# Revit family: Legrand Mini Colonnes clippage direct
name_source: partatom
category: Installations électriques
units: mm (PartAtom-declared; Revit-internal decimal feet)

## family parameters
Basée sur le plan de construction = Non
Conserver l'orientation des annotations = Non
Cote de connecteur circulaire = Utiliser le diamètre
Couper avec des vides une fois chargée = Non
Partagée = Non
Point de calcul de pièce = Non
Toujours verticalement = Oui
Type d'élément = Normal

## types (13) — shared parameters
Fabricant = LEGRAND
Standard = A clippage direct-ON
zero-valued in all types: Elévation par défaut

## per-type parameters (varying)
| type | 1 CPT | 2 CPT | 4 CPT | Black | Column stand | Description | Finition | H1 | HC | Largeur | Longueur | Matériau couvercle | Matériau principal | Matériaux corps | Modèle | Nombre de compartiments | Séparateur |
| Colonnette 1 cpt 45 0,30M BL | Oui | Non | Non | Non | Pied mobile : Pied pour Colonnettes Blanc | Colonnette a clippage direct 1 compartiment 0,30m Blanc | Blanc | 300 mm | 260 mm  [stored 0.853018 ft] | 75 mm  [stored 0.246063 ft] | 82 mm | Legrand - Plastique blanc | Aluminium | Legrand - Aluminium blanc | LG-653000 | 1 compartiment | 35 mm |
| Colonnette 1 cpt 45 0,30M Noir | Oui | Non | Non | Oui | Tablette : Table pour Colonnettes T1/2 | Colonnette a clippage direct 1 compartiment 0,30m Noir | Noir | 300 mm | 260 mm  [stored 0.853018 ft] | 75 mm  [stored 0.246063 ft] | 82 mm | Legrand - Plastique noir | Aluminium | Legrand - Aluminium noir | LG_653002 | 1 compartiment | 35 mm |
| Colonnette 1 cpt 45 0,68M BL | Oui | Non | Non | Non | Pied mobile : Pied pour Colonnettes Blanc | Colonnette a clippage direct 1 compartiment 0,68m Blanc | Blanc | 680 mm  [stored 2.23097 ft] | 640 mm  [stored 2.09974 ft] | 75 mm  [stored 0.246063 ft] | 82 mm | Legrand - Plastique blanc | Aluminium | Legrand - Aluminium blanc | LG-653003 | 1 compartiment | 35 mm |
| Colonnette 1 cpt 45 0,68M Noir | Oui | Non | Non | Oui | Tablette : Table pour Colonnettes T1/2 | Colonnette a clippage direct 1 compartiment 0,68m Noir | Noir | 680 mm  [stored 2.23097 ft] | 640 mm  [stored 2.09974 ft] | 75 mm  [stored 0.246063 ft] | 82 mm | Legrand - Plastique noir | Aluminium | Legrand - Aluminium noir | LG-653005 | 1 compartiment | 35 mm |
| Colonnette 2 cpts 45 0,3M BL | Non | Oui | Non | Non | Pied mobile : Pied pour Colonnettes Blanc | Colonnette a clippage direct 2 compartiments 0,30m Blanc | Blanc | 300 mm | 260 mm  [stored 0.853018 ft] | 75 mm  [stored 0.246063 ft] | 125 mm  [stored 0.410105 ft] | Legrand - Plastique blanc | Plastique | Legrand - Plastique blanc | LG-653020 | 2 compartiments | 35 mm |
| Colonnette 2 cpts 45 0,3M Noir | Non | Oui | Non | Oui | Tablette : Table pour Colonnettes T1/2 | Colonnette a clippage direct 2 compartiments 0,30m Noir | Noir | 300 mm | 260 mm  [stored 0.853018 ft] | 75 mm  [stored 0.246063 ft] | 125 mm  [stored 0.410105 ft] | Legrand - Plastique noir | Aluminium | Legrand - Aluminium noir | LG-653022 | 2 compartiments | 35 mm |
| Colonnette 2 cpts 45 0,68M Blanc | Non | Oui | Non | Non | Pied mobile : Pied pour Colonnettes Blanc | Colonnette a clippage direct 2 compartiments 0,68m Blanc | Blanc | 380 mm | 340 mm | 75 mm  [stored 0.246063 ft] | 125 mm  [stored 0.410105 ft] | Legrand - Plastique blanc | Aluminium | Legrand - Aluminium blanc | LG-653023 | 2 compartiments | 35 mm |
| Colonnette 2 cpt 45 0,68M Noir | Non | Oui | Non | Oui | Tablette : Table pour Colonnettes T1/2 | Colonnette a clippage direct 2 compartiments 0,68m Noir | Noir | 680 mm  [stored 2.23097 ft] | 640 mm  [stored 2.09974 ft] | 75 mm  [stored 0.246063 ft] | 125 mm  [stored 0.410105 ft] | Legrand - Plastique noir | Aluminium | Legrand - Aluminium noir | LG-653025 | 2 compartiments | 35 mm |
| Colonnette 4 cpts 45 0,30M Blanc | Non | Non | Oui | Non | Pied mobile : Pied pour Colonnettes Blanc | Colonnette a clippage direct 4 compartiments 0,30m Blanc | Blanc | 300 mm | 260 mm  [stored 0.853018 ft] | 125 mm  [stored 0.410105 ft] | 125 mm  [stored 0.410105 ft] | Legrand - Plastique blanc | Aluminium | Legrand - Aluminium blanc | LG-653040 | 4 compartiments | 125 mm  [stored 0.410105 ft] |
| Colonnette 4 cpts 45 0,30M Noir | Non | Non | Oui | Oui | Tablette : Table pour Colonnettes T1/2 | Colonnette a clippage direct 4 compartiments 0,30m Noir | Noir | 300 mm | 260 mm  [stored 0.853018 ft] | 125 mm  [stored 0.410105 ft] | 125 mm  [stored 0.410105 ft] | Legrand - Plastique noir | Aluminium | Legrand - Aluminium noir | LG-653042 | 4 compartiments | 125 mm  [stored 0.410105 ft] |
| Colonnette 4 cpt 45 0,68M Noir | Non | Non | Oui | Oui | Tablette : Table pour Colonnettes T1/2 | Colonnette a clippage direct 4 compartiments 0,68m Noir | Noir | 680 mm  [stored 2.23097 ft] | 640 mm  [stored 2.09974 ft] | 125 mm  [stored 0.410105 ft] | 125 mm  [stored 0.410105 ft] | Legrand - Plastique noir | Aluminium | Legrand - Aluminium noir | LG-653045 | 4 compartiments | 125 mm  [stored 0.410105 ft] |
| Colonnette 4 cpts 45 0,68M BL | Non | Non | Oui | Non | Pied mobile : Pied pour Colonnettes Blanc | Colonnette a clippage direct 4 compartiments 0,68m Blanc | Blanc | 680 mm  [stored 2.23097 ft] | 640 mm  [stored 2.09974 ft] | 125 mm  [stored 0.410105 ft] | 125 mm  [stored 0.410105 ft] | Legrand - Plastique blanc | Aluminium | Legrand - Aluminium blanc | LG-653043 | 4 compartiments | 125 mm  [stored 0.410105 ft] |
| Roll&Plug 2 cpts 0,68M Blanc | Non | Oui | Non | Non | Pied mobile : Pied pour Colonnettes Blanc | roll and plug 2 cpts 0,68m  table Blanc pied roulettes 6pc double usb 4m cordon | Blanc | 680 mm  [stored 2.23097 ft] | 640 mm  [stored 2.09974 ft] | 75 mm  [stored 0.246063 ft] | 125 mm  [stored 0.410105 ft] | Legrand - Plastique blanc | Aluminium | Legrand - Aluminium blanc | LG-653029 | 2 compartiments | 35 mm |

note: [stored X ft] marks values corroborated as IEEE doubles in the binary element streams (Revit-internal decimal feet)
